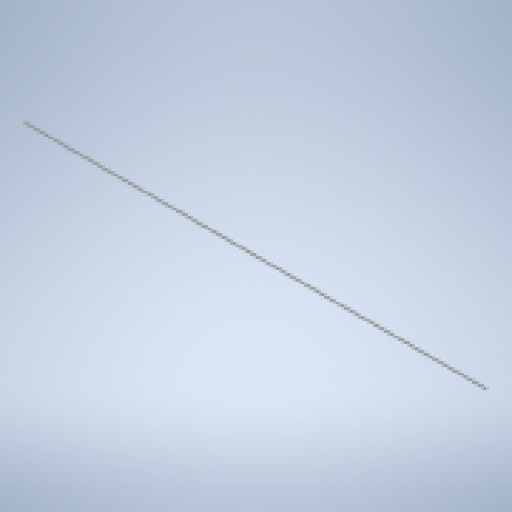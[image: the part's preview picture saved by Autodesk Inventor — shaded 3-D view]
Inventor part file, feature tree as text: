
AUTODESK INVENTOR PART (.ipt)
format: ipt  version: 2025 (Build 290162010, 162A)  size: 150,528 bytes
history: native  units: mm
features: extrude x1, sketch x1
ambient origin geometry x8: Origin, YZ Plane, XZ Plane, XY Plane, X Axis, Y Axis, Z Axis, Center Point
bodies: Volumenkörper1 (feature_tree)
feature tree (2):
  extrude  "Extrusion1"  Depth=447.0mm TaperAngle=0.0deg
  sketch  "Skizze1"  dims[d0=2.0mm d1=447.0mm d2=0.0mm]
